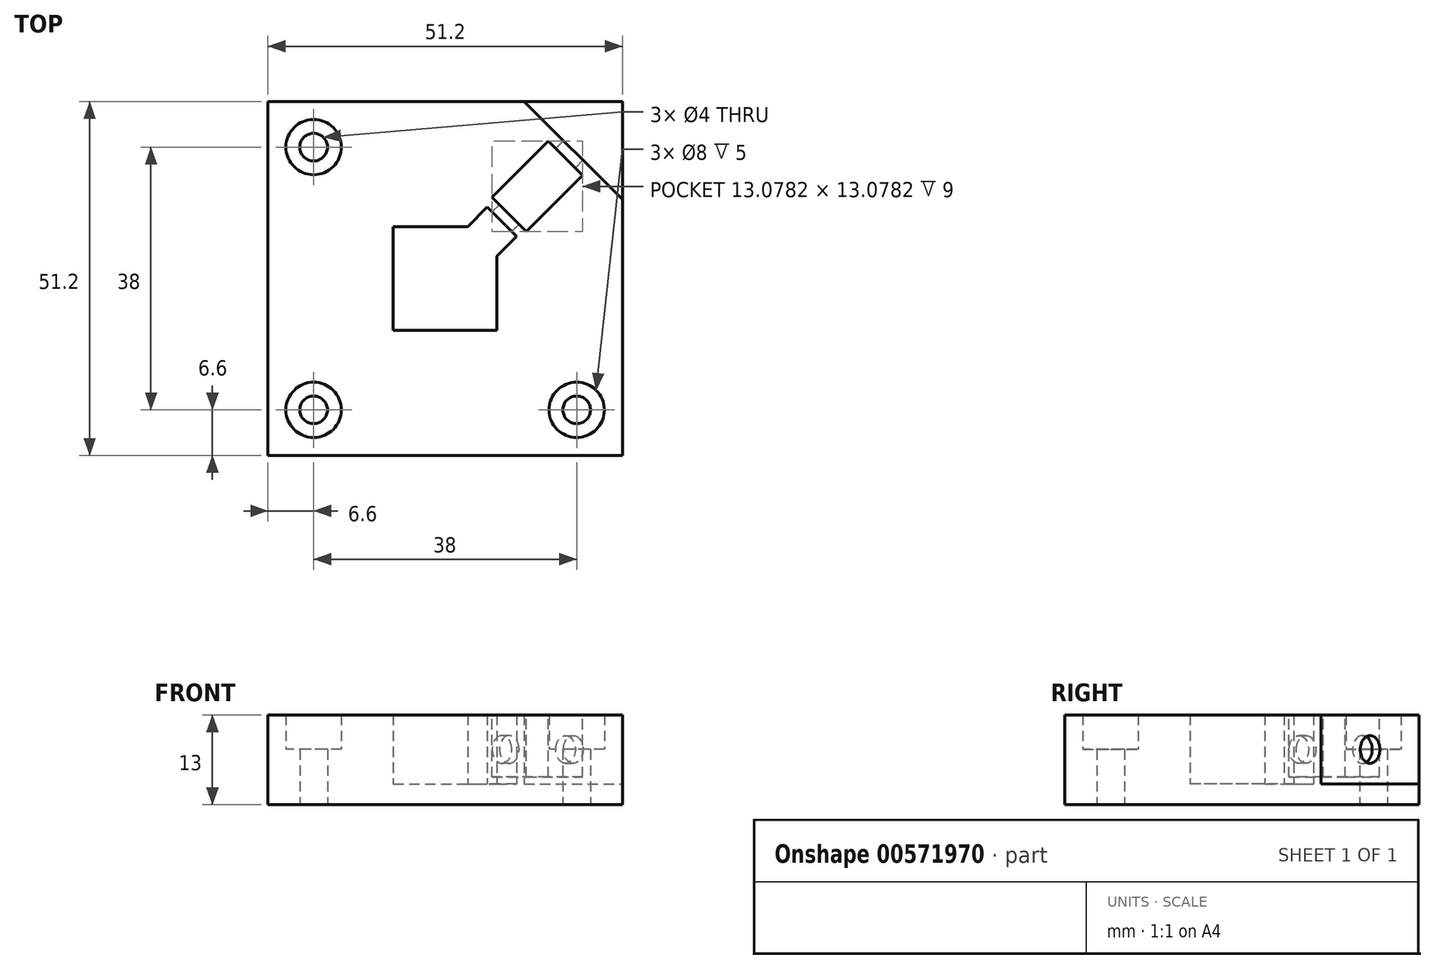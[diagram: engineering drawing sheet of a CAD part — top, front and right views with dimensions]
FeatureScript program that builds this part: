
annotation { "Feature Type Name" : "Feature", "Feature Type Description" : "" }
export const myFeature = defineFeature(function(context is Context, id is Id, definition is map)
    precondition{}
    {
        {
            var Q0;
            Q0=qCreatedBy(makeId("Top.planeOp"),FACE);
            var sketch = newSketch(context, id + "F0", { "sketchPlane" : qUnion([Q0])});
            skLineSegment(sketch, "E0.bottom", {"start": v(-25.6, 25.6) * mm, "end": v(25.6, 25.6) * mm});
            skLineSegment(sketch, "E0.top", {"start": v(-25.6, -25.6) * mm, "end": v(25.6, -25.6) * mm});
            skLineSegment(sketch, "E0.left", {"start": v(-25.6, 25.6) * mm, "end": v(-25.6, -25.6) * mm});
            skLineSegment(sketch, "E0.right", {"start": v(25.6, 25.6) * mm, "end": v(25.6, -25.6) * mm});
            skLineSegment(sketch, "E1", {"start": v(-25.6, 25.6) * mm, "end": v(25.6, -25.6) * mm, "construction": true});
            skLineSegment(sketch, "E2", {"start": v(-25.6, -25.6) * mm, "end": v(25.6, 25.6) * mm, "construction": true});
            skCircle(sketch, "E3", {"center": v(-19, 19) * mm, "radius": 2 * mm});
            skLineSegment(sketch, "E4", {"start": v(-19, 21) * mm, "end": v(-19, 25.6) * mm, "construction": true});
            skLineSegment(sketch, "E5", {"start": v(-21, 19) * mm, "end": v(-25.6, 19) * mm, "construction": true});
            skCircle(sketch, "E6.MirrorC", {"center": v(-19, -19) * mm, "radius": 2 * mm});
            skCircle(sketch, "E7.MirrorC", {"center": v(19, -19) * mm, "radius": 2 * mm});
            skSolve(sketch);
        }
        {
            var Q0;
            Q0=qSketchRegion(id+"F0",true);
            extrude(context, id + "F1", {"entities" : qUnion([Q0]), "depth" : 3 * mm, "offsetDistance" : 25 * mm});
        }
        {
            var Q0;
            Q0=makeQuery(id+"F1.opExtrude","CAP_FACE",FACE,{"disambiguationData":[OSD([sQuery(id+"F0.wireOp",EDGE,"E0.bottom"),sQuery(id+"F0.wireOp",EDGE,"E0.top"),sQuery(id+"F0.wireOp",EDGE,"E0.left"),sQuery(id+"F0.wireOp",EDGE,"E0.right"),sQuery(id+"F0.wireOp",EDGE,"E3"),sQuery(id+"F0.wireOp",EDGE,"E6.MirrorC"),sQuery(id+"F0.wireOp",EDGE,"a97bc87b-33af-4f80-ade9-4d20e9dde7b60.MirrorC"),sQuery(id+"F0.wireOp",EDGE,"E7.MirrorC")])],"isStart":false});
            var sketch = newSketch(context, id + "F2", { "sketchPlane" : qUnion([Q0])});
            skLineSegment(sketch, "E8.bottom", {"start": v(-7.5, 7.5) * mm, "end": v(3.26, 7.5) * mm});
            skLineSegment(sketch, "E8.top", {"start": v(-7.5, -7.5) * mm, "end": v(7.5, -7.5) * mm});
            skLineSegment(sketch, "E8.left", {"start": v(-7.5, 7.5) * mm, "end": v(-7.5, -7.5) * mm});
            skLineSegment(sketch, "E8.right", {"start": v(7.5, 3.26) * mm, "end": v(7.5, -7.5) * mm});
            skCircle(sketch, "E9", {"center": v(-19, 19) * mm, "radius": 2 * mm});
            skCircle(sketch, "E10.MirrorC", {"center": v(-19, -19) * mm, "radius": 2 * mm});
            skLineSegment(sketch, "E11.bottom", {"start": v(-25.6, 25.6) * mm, "end": v(11.4, 25.6) * mm});
            skLineSegment(sketch, "E11.top", {"start": v(-25.6, -25.6) * mm, "end": v(25.6, -25.6) * mm});
            skLineSegment(sketch, "E11.left", {"start": v(-25.6, 25.6) * mm, "end": v(-25.6, -25.6) * mm});
            skLineSegment(sketch, "E11.right", {"start": v(25.6, 11.4) * mm, "end": v(25.6, -25.6) * mm});
            skCircle(sketch, "E12.MirrorC", {"center": v(19, -19) * mm, "radius": 2 * mm});
            skLineSegment(sketch, "E13", {"start": v(11.4, 25.6) * mm, "end": v(25.6, 11.4) * mm});
            skLineSegment(sketch, "E14", {"start": v(3.26, 7.5) * mm, "end": v(6.09, 10.33) * mm});
            skLineSegment(sketch, "E15", {"start": v(7.5, 3.26) * mm, "end": v(10.33, 6.09) * mm});
            skLineSegment(sketch, "E16", {"start": v(10.33, 6.09) * mm, "end": v(6.09, 10.33) * mm});
            skPoint(sketch, "E17.orphan", {"position": v(7.5, 7.5) * mm});
            skSolve(sketch);
        }
        {
            var Q0;
            Q0=qSketchRegion(id+"F2",true);
            extrude(context, id + "F3", {"entities" : qUnion([Q0]), "operationType" : NewBodyOperationType.ADD, "depth" : 5 * mm, "offsetDistance" : 25 * mm});
        }
        {
            var Q0;
            Q0=makeQuery(id+"F3.opExtrude","CAP_FACE",FACE,{"disambiguationData":[OSD([sQuery(id+"F2.wireOp",EDGE,"d230b162-a4cc-462b-9001-7bc19fe26eac.bottom"),sQuery(id+"F2.wireOp",EDGE,"d230b162-a4cc-462b-9001-7bc19fe26eac.right"),sQuery(id+"F2.wireOp",EDGE,"c993e0fb-8ab3-41cd-a527-be316e8ff3e6"),sQuery(id+"F2.wireOp",EDGE,"b9f43957-481d-4778-b71d-99a2d851ea480.MirrorC"),sQuery(id+"F2.wireOp",EDGE,"e08a7d54-226c-4141-bf49-8684f58746d32.MirrorC"),sQuery(id+"F2.wireOp",EDGE,"e08a7d54-226c-4141-bf49-8684f58746d33.MirrorC"),sQuery(id+"F2.wireOp",EDGE,"e08a7d54-226c-4141-bf49-8684f58746d37.MirrorCS"),sQuery(id+"F2.wireOp",EDGE,"e08a7d54-226c-4141-bf49-8684f58746d38.MirrorCS"),sQuery(id+"F2.wireOp",EDGE,"E8.bottom"),sQuery(id+"F2.wireOp",EDGE,"E8.top"),sQuery(id+"F2.wireOp",EDGE,"E8.left"),sQuery(id+"F2.wireOp",EDGE,"E8.right")])],"isStart":false});
            var sketch = newSketch(context, id + "F4", { "sketchPlane" : qUnion([Q0])});
            skLineSegment(sketch, "E18.bottom", {"start": v(-25.6, 25.6) * mm, "end": v(11.4, 25.6) * mm});
            skLineSegment(sketch, "E18.top", {"start": v(-25.6, -25.6) * mm, "end": v(25.6, -25.6) * mm});
            skLineSegment(sketch, "E18.left", {"start": v(-25.6, 25.6) * mm, "end": v(-25.6, -25.6) * mm});
            skLineSegment(sketch, "E18.right", {"start": v(25.6, 11.4) * mm, "end": v(25.6, -25.6) * mm});
            skLineSegment(sketch, "E19.bottom", {"start": v(-7.5, 7.5) * mm, "end": v(3.26, 7.5) * mm});
            skLineSegment(sketch, "E19.top", {"start": v(-7.5, -7.5) * mm, "end": v(7.5, -7.5) * mm});
            skLineSegment(sketch, "E19.left", {"start": v(-7.5, 7.5) * mm, "end": v(-7.5, -7.5) * mm});
            skLineSegment(sketch, "E19.right", {"start": v(7.5, 3.26) * mm, "end": v(7.5, -7.5) * mm});
            skCircle(sketch, "E20", {"center": v(-19, 19) * mm, "radius": 4 * mm});
            skCircle(sketch, "E21.MirrorC", {"center": v(-19, -19) * mm, "radius": 4 * mm});
            skLineSegment(sketch, "E22", {"start": v(11.4, 25.6) * mm, "end": v(25.6, 11.4) * mm});
            skCircle(sketch, "E23.MirrorC", {"center": v(19, -19) * mm, "radius": 4 * mm});
            skLineSegment(sketch, "E24", {"start": v(3.26, 7.5) * mm, "end": v(6.09, 10.33) * mm});
            skLineSegment(sketch, "E25", {"start": v(6.09, 10.33) * mm, "end": v(10.33, 6.09) * mm});
            skLineSegment(sketch, "E26", {"start": v(10.33, 6.09) * mm, "end": v(7.5, 3.26) * mm});
            skSolve(sketch);
        }
        {
            var Q0;
            Q0=qSketchRegion(id+"F4",true);
            extrude(context, id + "F5", {"entities" : qUnion([Q0]), "operationType" : NewBodyOperationType.ADD, "depth" : 5 * mm, "offsetDistance" : 25 * mm});
        }
        {
            var Q0;
            Q0=makeQuery(id+"F5.boolean.opBoolean","MERGE",FACE,{"derivedFrom":[makeQuery(id+"F3.opExtrude","SWEPT_FACE",FACE,{"disambiguationData":[OSD([sQuery(id+"F2.wireOp",EDGE,"E13")])]}),makeQuery(id+"F5.opExtrude","SWEPT_FACE",FACE,{"disambiguationData":[OSD([sQuery(id+"F4.wireOp",EDGE,"E22")])]})]});
            var sketch = newSketch(context, id + "F6", { "sketchPlane" : qUnion([Q0])});
            skCircle(sketch, "E27", {"center": v(0, 8) * mm, "radius": 2 * mm});
            skLineSegment(sketch, "E28", {"start": v(10.04, 3) * mm, "end": v(-10.04, 13) * mm, "construction": true});
            skLineSegment(sketch, "E29", {"start": v(10.04, 13) * mm, "end": v(-10.04, 3) * mm, "construction": true});
            skSolve(sketch);
        }
        {
            var Q0;
            Q0 = qSketchRegion(id + "F6", true);
            extrude(context, id + "F7", {"entities" : qUnion([Q0]), "operationType" : NewBodyOperationType.REMOVE, "oppositeDirection" : true, "depth" : 2 * mm, "offsetDistance" : 25 * mm});
        }
        {
            var Q0;
            Q0=makeQuery(id+"F7.boolean.opBoolean","COPY",FACE,{"derivedFrom":makeQuery(id+"F7.opExtrude","CAP_FACE",FACE,{"disambiguationData":[OSD([sQuery(id+"F6.wireOp",EDGE,"E27")])],"isStart":false})});
            var sketch = newSketch(context, id + "F8", { "sketchPlane" : qUnion([Q0])});
            skCircle(sketch, "E30", {"center": v(0, 8) * mm, "radius": 3.5 * mm});
            skSolve(sketch);
        }
        {
            var Q0;
            Q0 = qSketchRegion(id + "F8", true);
            extrude(context, id + "F9", {"entities" : qUnion([Q0]), "operationType" : NewBodyOperationType.REMOVE, "oppositeDirection" : true, "depth" : 11 * mm, "offsetDistance" : 25 * mm});
        }
        {
            var Q0;
            Q0=makeQuery(id+"F5.boolean.opBoolean","MERGE",FACE,{"derivedFrom":[makeQuery(id+"F3.opExtrude","SWEPT_FACE",FACE,{"disambiguationData":[OSD([sQuery(id+"F2.wireOp",EDGE,"E16")])]}),makeQuery(id+"F5.opExtrude","SWEPT_FACE",FACE,{"disambiguationData":[OSD([sQuery(id+"F4.wireOp",EDGE,"E25")])]})]});
            var sketch = newSketch(context, id + "F10", { "sketchPlane" : qUnion([Q0])});
            skCircle(sketch, "E31", {"center": v(0, 8) * mm, "radius": 2 * mm});
            skPoint(sketch, "E31.centerSnap0", {"position": v(-3, 8) * mm});
            skSolve(sketch);
        }
        {
            var Q0;
            Q0 = qSketchRegion(id + "F10", true);
            extrude(context, id + "F11", {"entities" : qUnion([Q0]), "operationType" : NewBodyOperationType.REMOVE, "oppositeDirection" : true, "depth" : 4 * mm, "offsetDistance" : 25 * mm});
        }
        {
            var Q0;
            Q0=makeQuery(id+"F5.opExtrude","CAP_FACE",FACE,{"disambiguationData":[OSD([sQuery(id+"F4.wireOp",EDGE,"E18.bottom"),sQuery(id+"F4.wireOp",EDGE,"E18.top"),sQuery(id+"F4.wireOp",EDGE,"E18.left"),sQuery(id+"F4.wireOp",EDGE,"E18.right"),sQuery(id+"F4.wireOp",EDGE,"E19.bottom"),sQuery(id+"F4.wireOp",EDGE,"E19.top"),sQuery(id+"F4.wireOp",EDGE,"E19.left"),sQuery(id+"F4.wireOp",EDGE,"E19.right"),sQuery(id+"F4.wireOp",EDGE,"E20"),sQuery(id+"F4.wireOp",EDGE,"E21.MirrorC"),sQuery(id+"F4.wireOp",EDGE,"E22"),sQuery(id+"F4.wireOp",EDGE,"E23.MirrorC"),sQuery(id+"F4.wireOp",EDGE,"E24"),sQuery(id+"F4.wireOp",EDGE,"E25"),sQuery(id+"F4.wireOp",EDGE,"E26")])],"isStart":false});
            var sketch = newSketch(context, id + "F12", { "sketchPlane" : qUnion([Q0])});
            skLineSegment(sketch, "E32", {"start": v(6.8, 11.74) * mm, "end": v(11.74, 6.8) * mm});
            skLineSegment(sketch, "E33", {"start": v(11.74, 6.8) * mm, "end": v(19.87, 14.92) * mm});
            skLineSegment(sketch, "E34", {"start": v(19.87, 14.92) * mm, "end": v(14.92, 19.87) * mm});
            skLineSegment(sketch, "E35", {"start": v(14.92, 19.87) * mm, "end": v(6.8, 11.74) * mm});
            skSolve(sketch);
        }
        {
            var Q0;
            Q0 = qSketchRegion(id + "F12", true);
            extrude(context, id + "F13", {"entities" : qUnion([Q0]), "operationType" : NewBodyOperationType.REMOVE, "oppositeDirection" : true, "depth" : 9 * mm, "offsetDistance" : 25 * mm});
        }
    });
